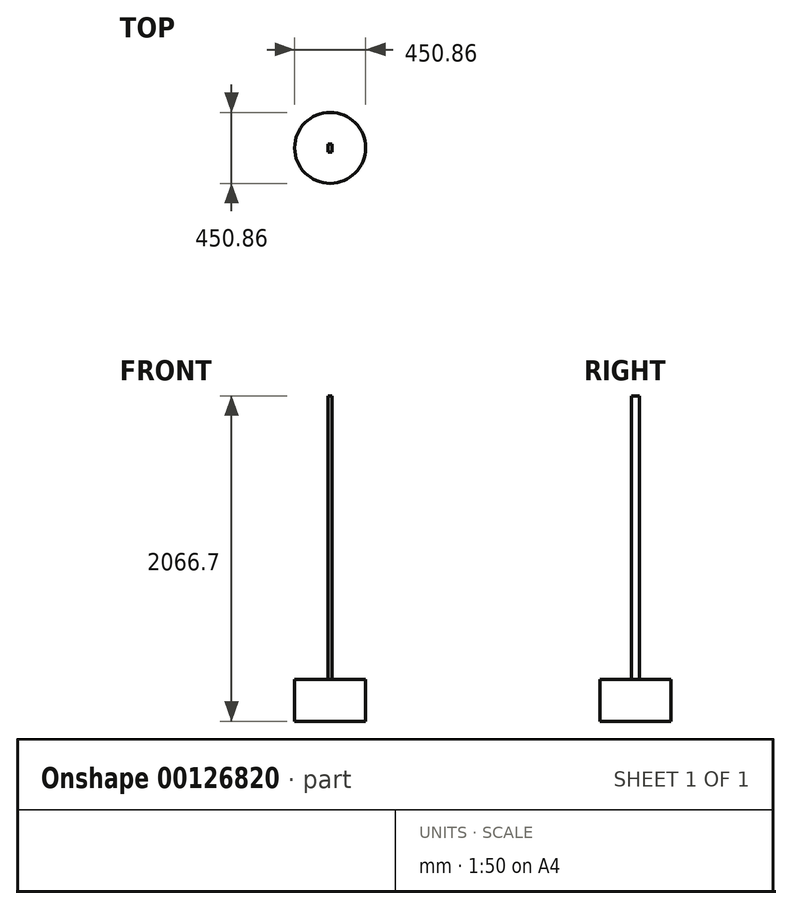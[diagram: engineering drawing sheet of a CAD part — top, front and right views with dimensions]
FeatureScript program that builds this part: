
annotation { "Feature Type Name" : "Feature", "Feature Type Description" : "" }
export const myFeature = defineFeature(function(context is Context, id is Id, definition is map)
    precondition{}
    {
        {
            var Q0;
            Q0=qCreatedBy(makeId("Top.planeOp"),FACE);
            var sketch = newSketch(context, id + "F0", { "sketchPlane" : qUnion([Q0])});
            skCircle(sketch, "E0", {"center": v(0, 0) * mm, "radius": 225.42 * mm});
            skSolve(sketch);
        }
        {
            var Q0;
            Q0=makeQuery(id+"F0.imprint","IMPRINT",FACE,{"disambiguationData":[TD([[makeQuery(id+"F0.imprint","IMPRINT",EDGE,{"derivedFrom":sQuery(id+"F0.wireOp",EDGE,"E0")}),1.0]])]});
            extrude(context, id + "F1", {"entities" : qUnion([Q0]), "depth" : 266.7 * mm});
        }
        {
            var Q0;
            Q0=makeQuery(id+"F1.opExtrude","CAP_FACE",FACE,{"disambiguationData":[OSD([sQuery(id+"F0.wireOp",EDGE,"E0")])],"isStart":false});
            var sketch = newSketch(context, id + "F2", { "sketchPlane" : qUnion([Q0])});
            skLineSegment(sketch, "E1.bottom", {"start": v(12.7, -25.4) * mm, "end": v(-12.7, -25.4) * mm});
            skLineSegment(sketch, "E1.top", {"start": v(12.7, 25.4) * mm, "end": v(-12.7, 25.4) * mm});
            skLineSegment(sketch, "E1.left", {"start": v(12.7, -25.4) * mm, "end": v(12.7, 25.4) * mm});
            skLineSegment(sketch, "E1.right", {"start": v(-12.7, -25.4) * mm, "end": v(-12.7, 25.4) * mm});
            skPoint(sketch, "E1.middle", {"position": v(0, 0) * mm});
            skSolve(sketch);
        }
        {
            var Q0;
            Q0=makeQuery(id+"F2.imprint","IMPRINT",FACE,{"disambiguationData":[TD([[makeQuery(id+"F2.imprint","IMPRINT",EDGE,{"derivedFrom":sQuery(id+"F2.wireOp",EDGE,"E1.bottom")}),-1.0]])]});
            extrude(context, id + "F3", {"entities" : qUnion([Q0]), "operationType" : NewBodyOperationType.ADD, "depth" : 1800 * mm});
        }
    });
